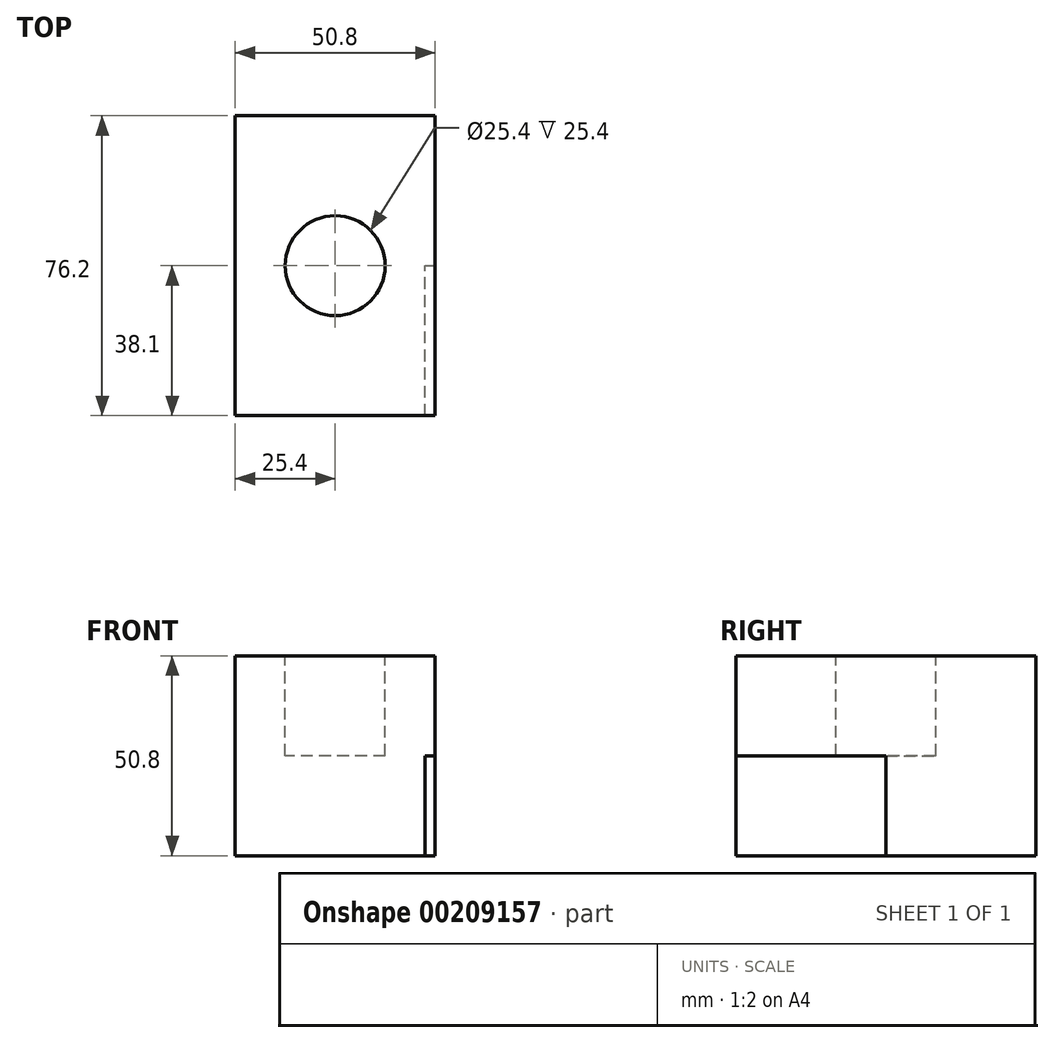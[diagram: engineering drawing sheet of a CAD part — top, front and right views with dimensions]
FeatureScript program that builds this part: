
annotation { "Feature Type Name" : "Feature", "Feature Type Description" : "" }
export const myFeature = defineFeature(function(context is Context, id is Id, definition is map)
    precondition{}
    {
        {
            var Q0;
            Q0=qCreatedBy(makeId("Top.planeOp"),FACE);
            var sketch = newSketch(context, id + "F0", { "sketchPlane" : qUnion([Q0])});
            skLineSegment(sketch, "E0.bottom", {"start": v(25.4, -38.1) * mm, "end": v(-25.4, -38.1) * mm});
            skLineSegment(sketch, "E0.top", {"start": v(25.4, 38.1) * mm, "end": v(-25.4, 38.1) * mm});
            skLineSegment(sketch, "E0.left", {"start": v(25.4, -38.1) * mm, "end": v(25.4, 38.1) * mm});
            skLineSegment(sketch, "E0.right", {"start": v(-25.4, -38.1) * mm, "end": v(-25.4, 38.1) * mm});
            skPoint(sketch, "E0.middle", {"position": v(0, 0) * mm});
            skSolve(sketch);
        }
        {
            var Q0;
            Q0 = qSketchRegion(id + "F0", true);
            extrude(context, id + "F1", {"entities" : qUnion([Q0]), "depth" : 50.8 * mm});
        }
        {
            var Q0;
            Q0=makeQuery(id+"F1.opExtrude","CAP_FACE",FACE,{"disambiguationData":[OSD([sQuery(id+"F0.wireOp",EDGE,"E0.bottom"),sQuery(id+"F0.wireOp",EDGE,"E0.top"),sQuery(id+"F0.wireOp",EDGE,"E0.left"),sQuery(id+"F0.wireOp",EDGE,"E0.right")])],"isStart":false});
            var sketch = newSketch(context, id + "F2", { "sketchPlane" : qUnion([Q0])});
            skCircle(sketch, "E1", {"center": v(0, 0) * mm, "radius": 12.7 * mm});
            skSolve(sketch);
        }
        {
            var Q0;
            Q0 = qSketchRegion(id + "F2", true);
            extrude(context, id + "F3", {"entities" : qUnion([Q0]), "operationType" : NewBodyOperationType.REMOVE, "oppositeDirection" : true, "depth" : 25.4 * mm});
        }
        {
            var Q0;
            Q0=makeQuery(id+"F1.opExtrude","SWEPT_FACE",FACE,{"disambiguationData":[OSD([sQuery(id+"F0.wireOp",EDGE,"E0.left")])]});
            var sketch = newSketch(context, id + "F4", { "sketchPlane" : qUnion([Q0])});
            skPoint(sketch, "E2.oppositeSnap0", {"position": v(-38.1, 25.4) * mm});
            skLineSegment(sketch, "E2.bottom", {"start": v(-38.1, 0) * mm, "end": v(0, 0) * mm});
            skLineSegment(sketch, "E2.top", {"start": v(-38.1, 25.4) * mm, "end": v(0, 25.4) * mm});
            skLineSegment(sketch, "E2.left", {"start": v(-38.1, 0) * mm, "end": v(-38.1, 25.4) * mm});
            skLineSegment(sketch, "E2.right", {"start": v(0, 0) * mm, "end": v(0, 25.4) * mm});
            skSolve(sketch);
        }
        {
            var Q0;
            Q0 = qSketchRegion(id + "F4", true);
            extrude(context, id + "F5", {"entities" : qUnion([Q0]), "operationType" : NewBodyOperationType.REMOVE, "oppositeDirection" : true, "depth" : 2.54 * mm});
        }
    });
